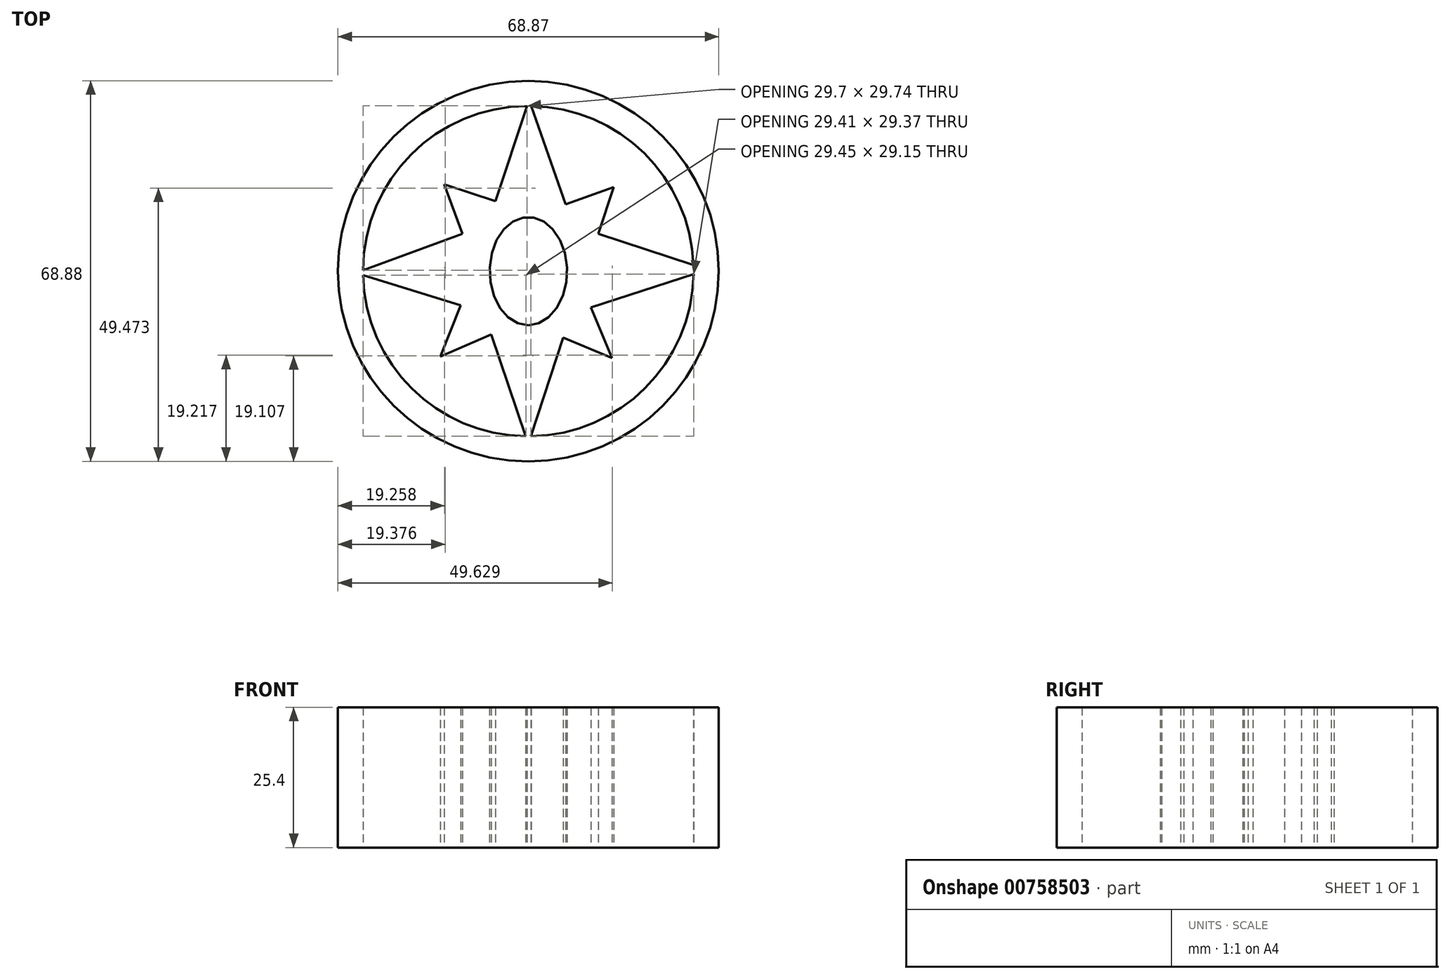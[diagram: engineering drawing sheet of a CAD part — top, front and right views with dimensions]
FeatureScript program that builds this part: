
annotation { "Feature Type Name" : "Feature", "Feature Type Description" : "" }
export const myFeature = defineFeature(function(context is Context, id is Id, definition is map)
    precondition{}
    {
        {
            var Q0;
            Q0=qCreatedBy(makeId("Top.planeOp"),FACE);
            var sketch = newSketch(context, id + "F0", { "sketchPlane" : qUnion([Q0])});
            skCircle(sketch, "E0", {"center": v(36.54, 37.3) * mm, "radius": 34.44 * mm});
            skArc(sketch, "E1", {"start": v(36.34, 67.2) * mm, "mid": v(15.38, 58.43) * mm, "end": v(6.64, 37.46) * mm});
            skEllipse(sketch, "E2", {"center": v(36.54, 37.3) * mm, "majorRadius": 7 * mm, "minorRadius": 9.8 * mm, "majorAxis": v(-1, 0)});
            skLineSegment(sketch, "E3", {"start": v(36.34, 67.2) * mm, "end": v(30.6, 49.95) * mm});
            skLineSegment(sketch, "E4", {"start": v(30.6, 49.95) * mm, "end": v(21.34, 53.02) * mm});
            skLineSegment(sketch, "E5", {"start": v(21.34, 53.02) * mm, "end": v(24.63, 44.06) * mm});
            skLineSegment(sketch, "E6", {"start": v(24.63, 44.06) * mm, "end": v(6.64, 37.46) * mm});
            skLineSegment(sketch, "E7", {"start": v(6.64, 36.54) * mm, "end": v(24.32, 31.12) * mm});
            skLineSegment(sketch, "E8", {"start": v(24.32, 31.12) * mm, "end": v(20.6, 21.82) * mm});
            skLineSegment(sketch, "E9", {"start": v(20.6, 21.82) * mm, "end": v(29.82, 25.85) * mm});
            skLineSegment(sketch, "E10", {"start": v(29.82, 25.85) * mm, "end": v(36.1, 7.4) * mm});
            skLineSegment(sketch, "E11", {"start": v(37.03, 7.4) * mm, "end": v(42.88, 25.28) * mm});
            skLineSegment(sketch, "E12", {"start": v(42.88, 25.28) * mm, "end": v(51.68, 21.6) * mm});
            skLineSegment(sketch, "E13", {"start": v(51.68, 21.6) * mm, "end": v(47.88, 30.76) * mm});
            skLineSegment(sketch, "E14", {"start": v(47.88, 30.76) * mm, "end": v(66.45, 36.76) * mm});
            skLineSegment(sketch, "E15", {"start": v(66.43, 38.38) * mm, "end": v(49.21, 44.07) * mm});
            skLineSegment(sketch, "E16", {"start": v(49.21, 44.07) * mm, "end": v(52, 52.53) * mm});
            skLineSegment(sketch, "E17", {"start": v(52, 52.53) * mm, "end": v(43.3, 49.38) * mm});
            skLineSegment(sketch, "E18", {"start": v(43.3, 49.38) * mm, "end": v(37.08, 67.2) * mm});
            skArc(sketch, "E19.trimOffspring", {"start": v(6.64, 36.54) * mm, "mid": v(15.5, 16.04) * mm, "end": v(36.1, 7.4) * mm});
            skArc(sketch, "E20.trimOffspring", {"start": v(37.03, 7.4) * mm, "mid": v(57.67, 16.13) * mm, "end": v(66.45, 36.76) * mm});
            skArc(sketch, "E21.trimOffspring", {"start": v(66.43, 38.38) * mm, "mid": v(57.5, 58.64) * mm, "end": v(37.08, 67.2) * mm});
            skSolve(sketch);
        }
        {
            var Q0;
            Q0=makeQuery(id+"F0.imprint","IMPRINT",FACE,{"disambiguationData":[TD([[makeQuery(id+"F0.imprint","IMPRINT",EDGE,{"derivedFrom":sQuery(id+"F0.wireOp",EDGE,"E0")}),1.0]])]});
            extrude(context, id + "F1", {"entities" : qUnion([Q0]), "depth" : 25.4 * mm, "offsetDistance" : 25.4 * mm});
        }
    });
